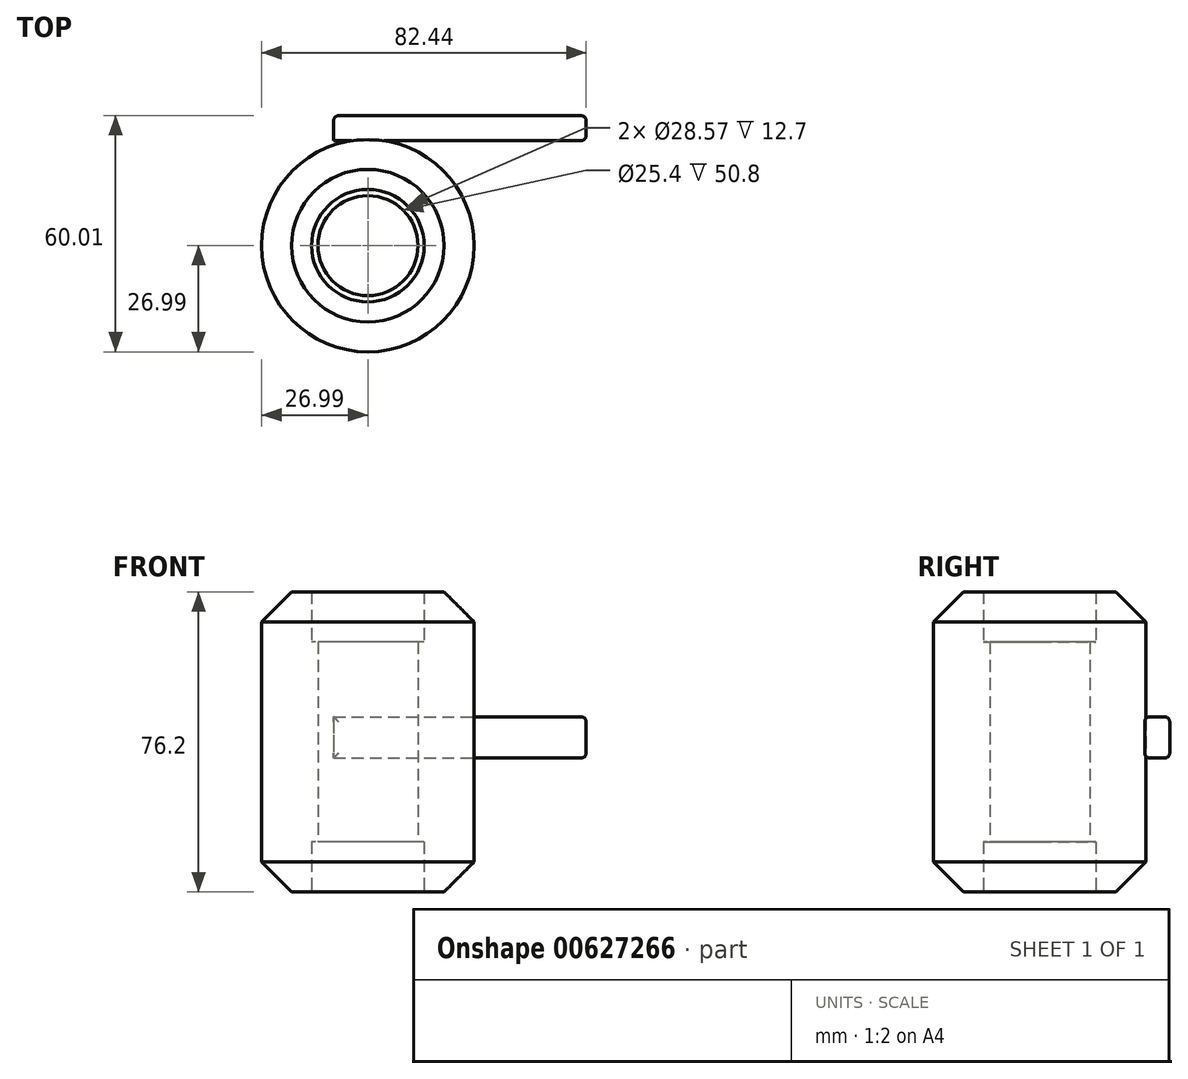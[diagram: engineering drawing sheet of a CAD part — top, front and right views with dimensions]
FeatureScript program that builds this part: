
annotation { "Feature Type Name" : "Feature", "Feature Type Description" : "" }
export const myFeature = defineFeature(function(context is Context, id is Id, definition is map)
    precondition{}
    {
        {
            var Q0;
            Q0=qCreatedBy(makeId("Top.planeOp"),FACE);
            var sketch = newSketch(context, id + "F0", { "sketchPlane" : qUnion([Q0])});
            skLineSegment(sketch, "E0", {"start": v(0, 0) * mm, "end": v(12.7, 0) * mm});
            skCircle(sketch, "E1", {"center": v(0, 0) * mm, "radius": 12.7 * mm});
            skCircle(sketch, "E2.0", {"center": v(0, 0) * mm, "radius": 14.29 * mm});
            skSolve(sketch);
        }
        {
            var Q0;
            Q0=qCreatedBy(makeId("Top.planeOp"),FACE);
            var sketch = newSketch(context, id + "F1", { "sketchPlane" : qUnion([Q0])});
            skSolve(sketch);
        }
        {
            var Q0;
            Q0=qSketchRegion(id+"F1",true);
            var Q1;
            Q1=makeQuery(id+"F0.imprint","IMPRINT",FACE,{"disambiguationData":[TD([[makeQuery(id+"F0.imprint","IMPRINT",EDGE,{"derivedFrom":sQuery(id+"F0.wireOp",EDGE,"E1")}),-1.0]])]});
            extrude(context, id + "F2", {"entities" : qUnion([Q0, Q1]), "depth" : 50.8 * mm, "offsetDistance" : 25.4 * mm});
        }
        {
            var Q0;
            Q0=qSketchRegion(id+"F0",true);
            var sketch = newSketch(context, id + "F3", { "sketchPlane" : qUnion([Q0])});
            skCircle(sketch, "E3.0", {"center": v(0, 0) * mm, "radius": 26.99 * mm});
            skSolve(sketch);
        }
        {
            var Q0;
            Q0=makeQuery(id+"F3.imprint","IMPRINT",FACE,{"disambiguationData":[TD([[makeQuery(id+"F3.imprint","IMPRINT",EDGE,{"derivedFrom":sQuery(id+"F3.wireOp",EDGE,"E3.0")}),1.0]])]});
            var Q1;
            Q1=sQuery(id+"F0.wireOp",EDGE,"E2.0");
            var Q2;
            Q2=sQuery(id+"F3.wireOp",EDGE,"E3.0");
            extrude(context, id + "F4", {"entities" : qUnion([Q0]), "operationType" : NewBodyOperationType.ADD, "surfaceEntities" : qUnion([Q1, Q2]), "depth" : 63.5 * mm, "offsetDistance" : 25.4 * mm, "hasSecondDirection" : true, "secondDirectionOppositeDirection" : true, "secondDirectionDepth" : 12.7 * mm});
        }
        {
            var Q0;
            Q0=makeQuery(id+"F4.opExtrude","CAP_EDGE",EDGE,{"disambiguationData":[OSD([sQuery(id+"F3.wireOp",EDGE,"E3.0")])],"isStart":false});
            var Q1;
            Q1=makeQuery(id+"F4.opExtrude","CAP_EDGE",EDGE,{"disambiguationData":[OSD([sQuery(id+"F3.wireOp",EDGE,"E3.0")])],"isStart":true});
            chamfer(context, id + "F5", {"entities" : qUnion([Q0, Q1]), "width" : 7.62 * mm, "tangentPropagation" : true});
        }
        {
            var Q0;
            Q0=qCreatedBy(makeId("Front.planeOp"),FACE);
            var sketch = newSketch(context, id + "F6", { "sketchPlane" : qUnion([Q0])});
            skLineSegment(sketch, "E4.bottom", {"start": v(-8.7, 31.78) * mm, "end": v(55.45, 31.78) * mm});
            skLineSegment(sketch, "E4.top", {"start": v(-8.7, 21.3) * mm, "end": v(55.45, 21.3) * mm});
            skLineSegment(sketch, "E4.left", {"start": v(-8.7, 31.78) * mm, "end": v(-8.7, 21.3) * mm});
            skLineSegment(sketch, "E4.right", {"start": v(55.45, 31.78) * mm, "end": v(55.45, 21.3) * mm});
            skSolve(sketch);
        }
        {
            var Q0;
            Q0=qSketchRegion(id+"FStmFrAZIaOWUlX_1",true);
            var Q1;
            {var subQ0=sQuery(id+"FYjZxIcEohR0Ynb_1.wireOp",EDGE,"443e18fd-1d04-4f57-b39d-10a9bfe42ac6");var subQ1=makeQuery(id+"FYjZxIcEohR0Ynb_1.imprint","INTERSECT",VERTEX,{"derivedFrom":[subQ0,sQuery(id+"FYjZxIcEohR0Ynb_1.wireOp",EDGE,"c501c783-0ef8-4ae8-b3d2-48140e7115dc")]});Q1=makeQuery(id+"FYjZxIcEohR0Ynb_1.imprint","IMPRINT",FACE,{"disambiguationData":[TD([[makeQuery(id+"FYjZxIcEohR0Ynb_1.imprint","IMPRINT",EDGE,{"disambiguationData":[TD([[subQ1,1.0]])],"derivedFrom":subQ0}),1.0]])]});}
            var Q2;
            {var subQ0=sQuery(id+"FYjZxIcEohR0Ynb_1.wireOp",EDGE,"c501c783-0ef8-4ae8-b3d2-48140e7115dc");Q2=makeQuery(id+"FYjZxIcEohR0Ynb_1.imprint","IMPRINT",FACE,{"disambiguationData":[TD([[makeQuery(id+"FYjZxIcEohR0Ynb_1.imprint","IMPRINT",EDGE,{"derivedFrom":subQ0}),-1.0]])]});}
            var Q3;
            {var subQ0=sQuery(id+"FYjZxIcEohR0Ynb_1.wireOp",EDGE,"9c8fd01a-dc82-46a9-a018-ea8be588cb86");var subQ1=makeQuery(id+"FYjZxIcEohR0Ynb_1.imprint","INTERSECT",VERTEX,{"derivedFrom":[subQ0,sQuery(id+"FYjZxIcEohR0Ynb_1.wireOp",EDGE,"c501c783-0ef8-4ae8-b3d2-48140e7115dc")]});Q3=makeQuery(id+"FYjZxIcEohR0Ynb_1.imprint","IMPRINT",FACE,{"disambiguationData":[TD([[makeQuery(id+"FYjZxIcEohR0Ynb_1.imprint","IMPRINT",EDGE,{"disambiguationData":[TD([[subQ1,1.0]])],"derivedFrom":subQ0}),1.0]])]});}
            var Q4;
            Q4=makeQuery(id+"F6.imprint","IMPRINT",FACE,{"disambiguationData":[TD([[makeQuery(id+"F6.imprint","IMPRINT",EDGE,{"derivedFrom":sQuery(id+"F6.wireOp",EDGE,"E4.bottom")}),-1.0]])]});
            extrude(context, id + "F7", {"entities" : qUnion([Q0, Q1, Q2, Q3, Q4]), "oppositeDirection" : true, "depth" : 33.02 * mm, "offsetDistance" : 25.4 * mm, "hasSecondDirection" : true, "secondDirectionOppositeDirection" : true, "secondDirectionDepth" : 26.67 * mm});
        }
        {
            var Q0;
            Q0=makeQuery(id+"F7.opExtrude","CAP_FACE",FACE,{"disambiguationData":[OSD([sQuery(id+"FStmFrAZIaOWUlX_1.wireOp",EDGE,"d14eafb9-cce9-403a-aaa2-bab3b7104b2c"),sQuery(id+"FStmFrAZIaOWUlX_1.wireOp",EDGE,"6d46858e-4966-4d5c-8c4b-00c8f02e4e6a"),sQuery(id+"FStmFrAZIaOWUlX_1.wireOp",EDGE,"b46cb536-2e7f-4ca6-bc0b-a31964254d72"),sQuery(id+"FStmFrAZIaOWUlX_1.wireOp",EDGE,"c3dd68a3-9125-4db1-9f63-96c839669f2c")])],"isStart":false});
            var Q1;
            Q1=makeQuery(id+"F7.opExtrude","CAP_EDGE",EDGE,{"disambiguationData":[OSD([sQuery(id+"F6.wireOp",EDGE,"E4.bottom")])],"isStart":false});
            var Q2;
            Q2=makeQuery(id+"F7.opExtrude","CAP_EDGE",EDGE,{"disambiguationData":[OSD([sQuery(id+"F6.wireOp",EDGE,"E4.top")])],"isStart":false});
            var Q3;
            Q3=makeQuery(id+"F7.opExtrude","CAP_EDGE",EDGE,{"disambiguationData":[OSD([sQuery(id+"F6.wireOp",EDGE,"E4.left")])],"isStart":false});
            var Q4;
            Q4=makeQuery(id+"F7.opExtrude","CAP_EDGE",EDGE,{"disambiguationData":[OSD([sQuery(id+"F6.wireOp",EDGE,"E4.top")])],"isStart":true});
            var Q5;
            Q5=makeQuery(id+"F7.opExtrude","CAP_EDGE",EDGE,{"disambiguationData":[OSD([sQuery(id+"F6.wireOp",EDGE,"E4.bottom")])],"isStart":true});
            var Q6;
            Q6=makeQuery(id+"F7.opExtrude","CAP_EDGE",EDGE,{"disambiguationData":[OSD([sQuery(id+"F6.wireOp",EDGE,"E4.right")])],"isStart":true});
            var Q7;
            Q7=makeQuery(id+"F7.opExtrude","SWEPT_EDGE",EDGE,{"disambiguationData":[OSD([sQuery(id+"F6.wireOp",EDGE,"E4.bottom"),sQuery(id+"F6.wireOp",EDGE,"E4.right")])]});
            var Q8;
            Q8=makeQuery(id+"F7.opExtrude","CAP_EDGE",EDGE,{"disambiguationData":[OSD([sQuery(id+"F6.wireOp",EDGE,"E4.right")])],"isStart":false});
            var Q9;
            Q9=makeQuery(id+"F7.opExtrude","SWEPT_EDGE",EDGE,{"disambiguationData":[OSD([sQuery(id+"F6.wireOp",EDGE,"E4.top"),sQuery(id+"F6.wireOp",EDGE,"E4.right")])]});
            fillet(context, id + "F8", {"entities" : qUnion([Q0, Q1, Q2, Q3, Q4, Q5, Q6, Q7, Q8, Q9]), "radius" : 1.27 * mm, "tangentPropagation" : true, "allowEdgeOverflow" : false});
        }
    });
